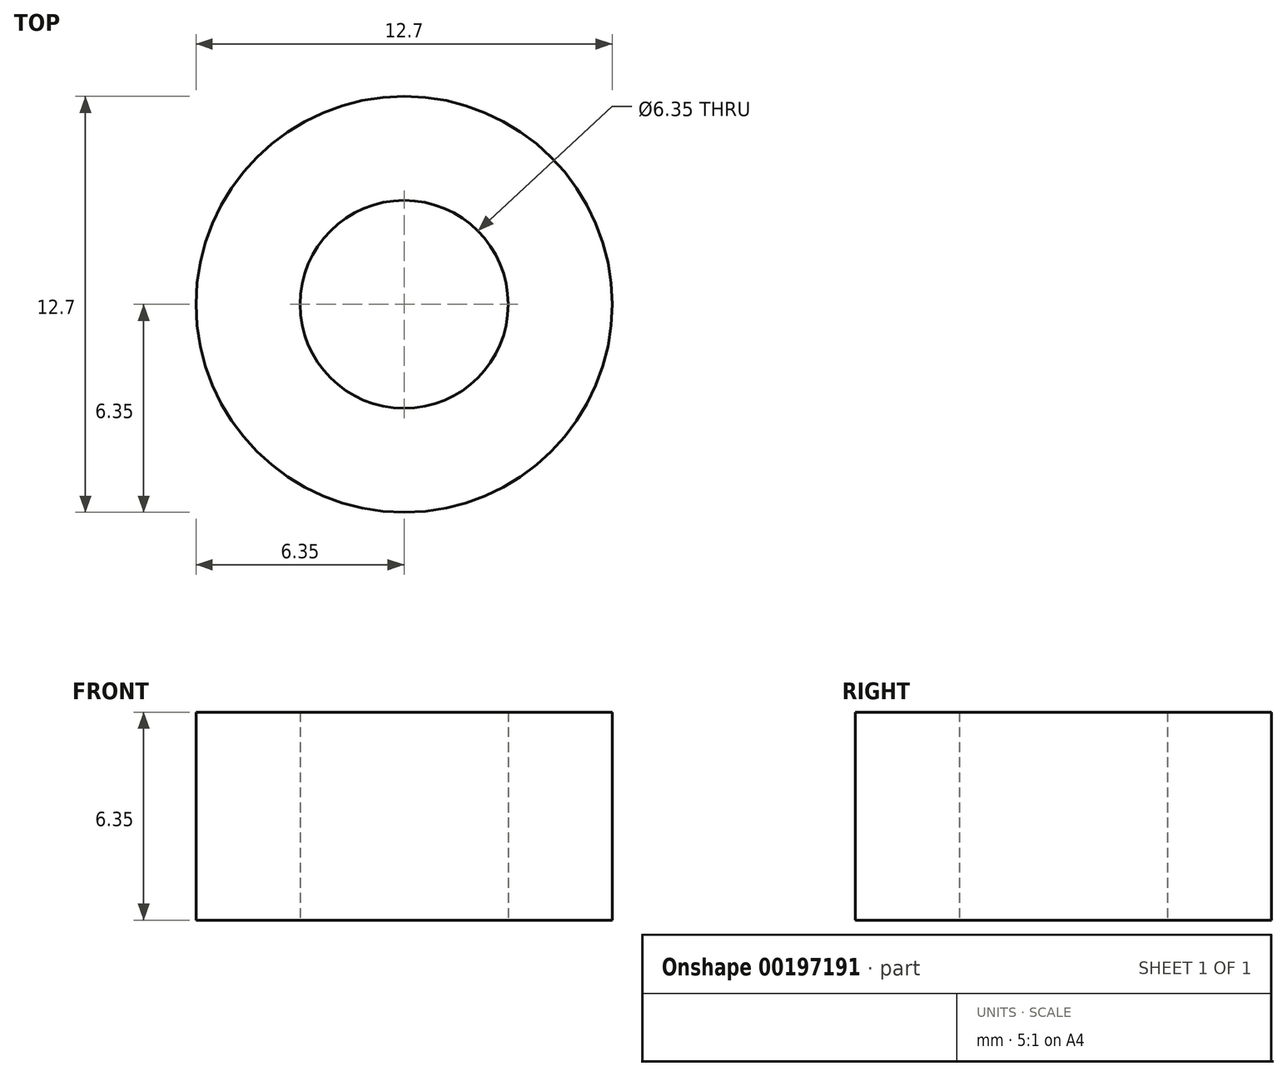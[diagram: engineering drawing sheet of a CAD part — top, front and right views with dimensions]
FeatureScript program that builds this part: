
annotation { "Feature Type Name" : "Feature", "Feature Type Description" : "" }
export const myFeature = defineFeature(function(context is Context, id is Id, definition is map)
    precondition{}
    {
        {
            var Q0;
            Q0=qCreatedBy(makeId("Top.planeOp"),FACE);
            var sketch = newSketch(context, id + "F0", { "sketchPlane" : qUnion([Q0])});
            skCircle(sketch, "E0", {"center": v(0, 0) * mm, "radius": 6.35 * mm});
            skCircle(sketch, "E1", {"center": v(0, 0) * mm, "radius": 3.18 * mm});
            skSolve(sketch);
        }
        {
            var Q0;
            Q0 = qSketchRegion(id + "F0", true);
            extrude(context, id + "F1", {"entities" : qUnion([Q0]), "depth" : 6.35 * mm});
        }
    });
